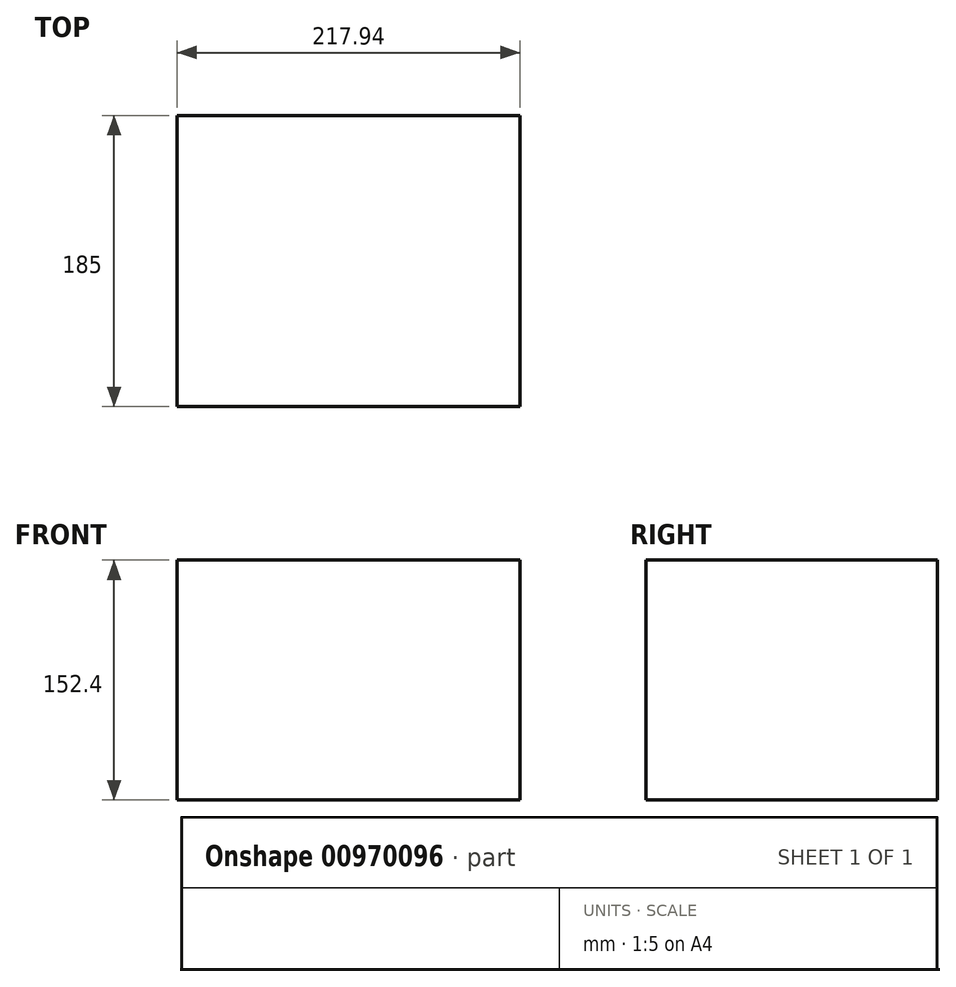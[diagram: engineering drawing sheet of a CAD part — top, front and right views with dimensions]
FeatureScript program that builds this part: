
annotation { "Feature Type Name" : "Feature", "Feature Type Description" : "" }
export const myFeature = defineFeature(function(context is Context, id is Id, definition is map)
    precondition{}
    {
        {
            var Q0;
            Q0=qCreatedBy(makeId("Top.planeOp"),FACE);
            var sketch = newSketch(context, id + "F0", { "sketchPlane" : qUnion([Q0])});
            skLineSegment(sketch, "E0.bottom", {"start": v(108.97, -92.5) * mm, "end": v(-108.97, -92.5) * mm});
            skLineSegment(sketch, "E0.top", {"start": v(108.97, 92.5) * mm, "end": v(-108.97, 92.5) * mm});
            skLineSegment(sketch, "E0.left", {"start": v(108.97, -92.5) * mm, "end": v(108.97, 92.5) * mm});
            skLineSegment(sketch, "E0.right", {"start": v(-108.97, -92.5) * mm, "end": v(-108.97, 92.5) * mm});
            skPoint(sketch, "E0.middle", {"position": v(0, 0) * mm});
            skSolve(sketch);
        }
        {
            var Q0;
            Q0 = qSketchRegion(id + "F0", true);
            extrude(context, id + "F1", {"entities" : qUnion([Q0]), "depth" : 152.4 * mm, "offsetDistance" : 25.4 * mm});
        }
    });
